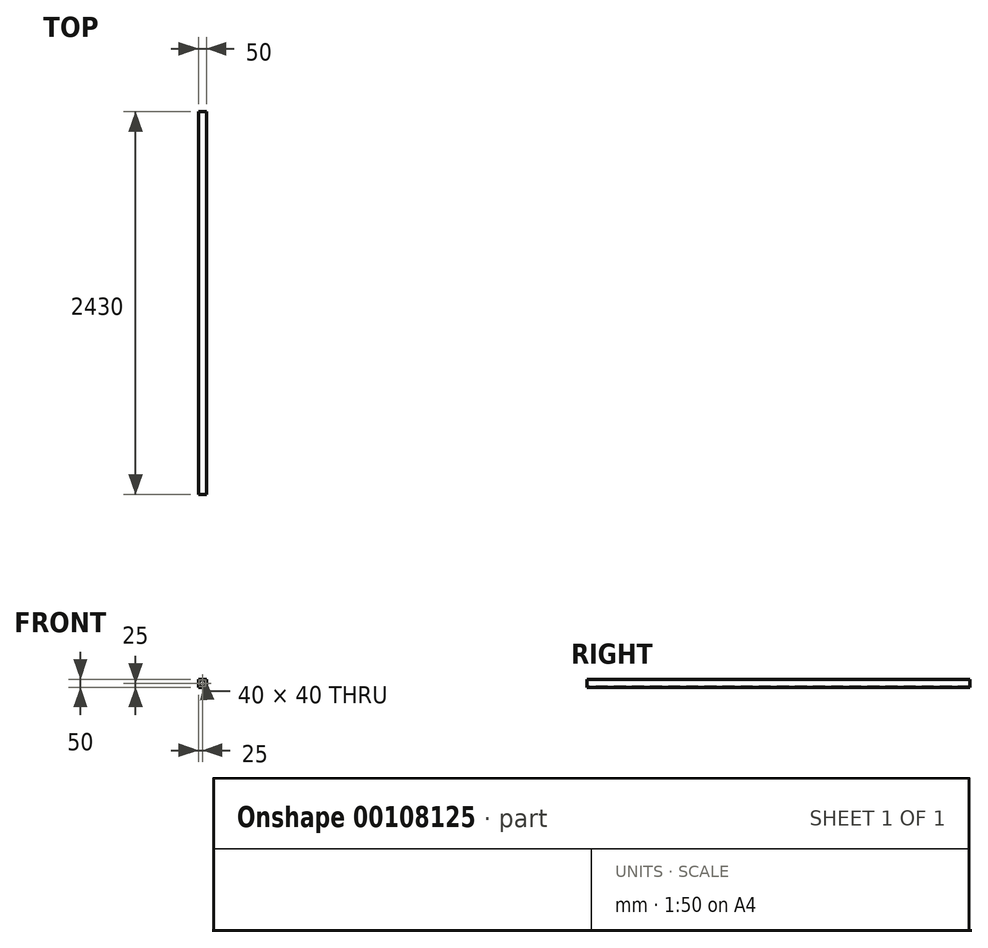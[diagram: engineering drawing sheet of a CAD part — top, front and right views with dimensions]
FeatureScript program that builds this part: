
annotation { "Feature Type Name" : "Feature", "Feature Type Description" : "" }
export const myFeature = defineFeature(function(context is Context, id is Id, definition is map)
    precondition{}
    {
        {
            var Q0;
            Q0=qCreatedBy(makeId("Front.planeOp"),FACE);
            var sketch = newSketch(context, id + "F0", { "sketchPlane" : qUnion([Q0])});
            skLineSegment(sketch, "E0.bottom", {"start": v(25, -25) * mm, "end": v(-25, -25) * mm});
            skLineSegment(sketch, "E0.top", {"start": v(25, 25) * mm, "end": v(-25, 25) * mm});
            skLineSegment(sketch, "E0.left", {"start": v(25, -25) * mm, "end": v(25, 25) * mm});
            skLineSegment(sketch, "E0.right", {"start": v(-25, -25) * mm, "end": v(-25, 25) * mm});
            skPoint(sketch, "E0.middle", {"position": v(0, 0) * mm});
            skLineSegment(sketch, "E1.bottom", {"start": v(20, -20) * mm, "end": v(-20, -20) * mm});
            skLineSegment(sketch, "E1.top", {"start": v(20, 20) * mm, "end": v(-20, 20) * mm});
            skLineSegment(sketch, "E1.left", {"start": v(20, -20) * mm, "end": v(20, 20) * mm});
            skLineSegment(sketch, "E1.right", {"start": v(-20, -20) * mm, "end": v(-20, 20) * mm});
            skSolve(sketch);
        }
        {
            var Q0;
            Q0=makeQuery(id+"F0.imprint","IMPRINT",FACE,{"disambiguationData":[TD([[makeQuery(id+"F0.imprint","IMPRINT",EDGE,{"derivedFrom":sQuery(id+"F0.wireOp",EDGE,"E0.bottom")}),-1.0]])]});
            extrude(context, id + "F1", {"entities" : qUnion([Q0]), "oppositeDirection" : true, "depth" : 2430 * mm});
        }
    });
